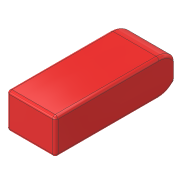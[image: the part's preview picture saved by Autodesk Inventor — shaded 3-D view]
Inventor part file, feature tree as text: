
AUTODESK INVENTOR PART (.ipt)
format: ipt  version: 2019.4 (Build 234330000, 330)  size: 120,320 bytes
history: native  units: mm
features: other x1, extrude x1, fillet x1, sketch x1
ambient origin geometry x8: Origin, YZ Plane, XZ Plane, XY Plane, X Axis, Y Axis, Z Axis, Center Point
bodies: Body1 (feature_tree)
feature tree (4):
  other  "ソリッド1"
  extrude  "押し出し1"  Depth=85.0mm
  fillet  "フィレット1"  Radius=25.5mm
  sketch  "スケッチ1"
